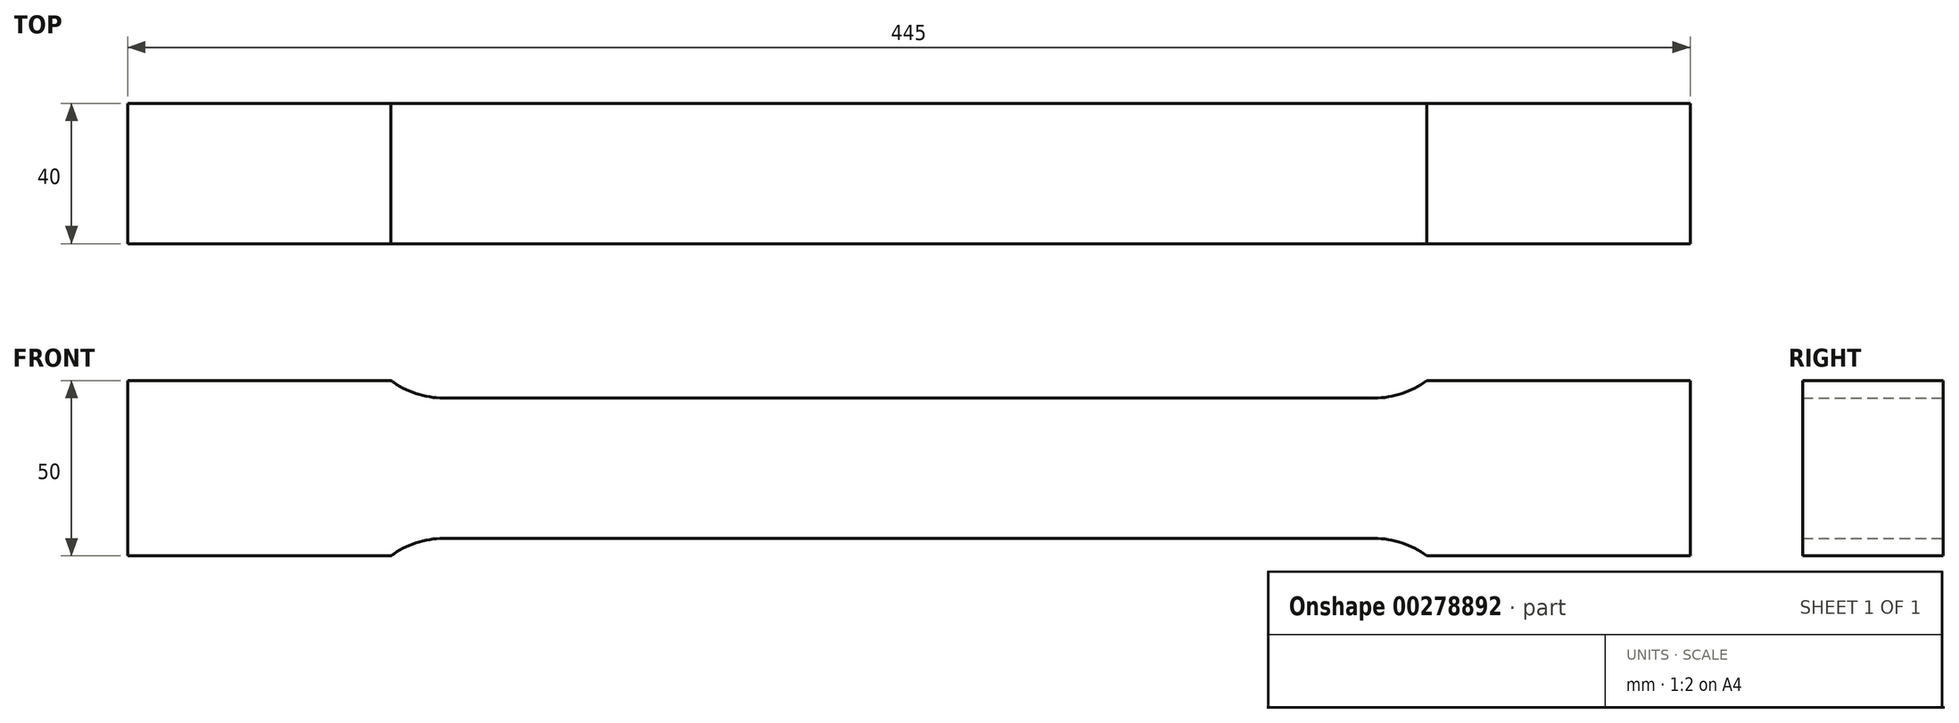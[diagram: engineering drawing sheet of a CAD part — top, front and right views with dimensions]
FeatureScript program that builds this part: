
annotation { "Feature Type Name" : "Feature", "Feature Type Description" : "" }
export const myFeature = defineFeature(function(context is Context, id is Id, definition is map)
    precondition{}
    {
        {
            var Q0;
            Q0=qCreatedBy(makeId("Front.planeOp"),FACE);
            var sketch = newSketch(context, id + "F0", { "sketchPlane" : qUnion([Q0])});
            skLineSegment(sketch, "E0", {"start": v(0, 20) * mm, "end": v(132.5, 20) * mm});
            skArc(sketch, "E1", {"start": v(132.5, 20) * mm, "mid": v(140.4, 21.28) * mm, "end": v(147.5, 25) * mm});
            skLineSegment(sketch, "E2", {"start": v(147.5, 25) * mm, "end": v(222.5, 25) * mm});
            skLineSegment(sketch, "E3", {"start": v(222.5, 25) * mm, "end": v(222.5, 0) * mm});
            skLineSegment(sketch, "E4.MirrorCS", {"start": v(0, -20) * mm, "end": v(132.5, -20) * mm});
            skLineSegment(sketch, "E5.MirrorCS", {"start": v(222.5, -25) * mm, "end": v(222.5, 0) * mm});
            skLineSegment(sketch, "E6.MirrorCS", {"start": v(147.5, -25) * mm, "end": v(222.5, -25) * mm});
            skArc(sketch, "E7.MirrorCS", {"start": v(132.5, -20) * mm, "mid": v(140.4, -21.28) * mm, "end": v(147.5, -25) * mm});
            skArc(sketch, "E8.MirrorCS", {"start": v(-132.5, -20) * mm, "mid": v(-140.4, -21.28) * mm, "end": v(-147.5, -25) * mm});
            skLineSegment(sketch, "E9.MirrorCS", {"start": v(-147.5, -25) * mm, "end": v(-222.5, -25) * mm});
            skArc(sketch, "E10.MirrorCS", {"start": v(-132.5, 20) * mm, "mid": v(-140.4, 21.28) * mm, "end": v(-147.5, 25) * mm});
            skLineSegment(sketch, "E11.MirrorCS", {"start": v(-147.5, 25) * mm, "end": v(-222.5, 25) * mm});
            skLineSegment(sketch, "E12.MirrorCS", {"start": v(-222.5, -25) * mm, "end": v(-222.5, 0) * mm});
            skLineSegment(sketch, "E13.MirrorCS", {"start": v(0, -20) * mm, "end": v(-132.5, -20) * mm});
            skLineSegment(sketch, "E14.MirrorCS", {"start": v(-222.5, 25) * mm, "end": v(-222.5, 0) * mm});
            skLineSegment(sketch, "E15.MirrorCS", {"start": v(0, 20) * mm, "end": v(-132.5, 20) * mm});
            skSolve(sketch);
        }
        {
            var Q0;
            Q0 = qSketchRegion(id + "F0", true);
            extrude(context, id + "F1", {"entities" : qUnion([Q0]), "endBound" : BoundingType.SYMMETRIC, "depth" : 40 * mm});
        }
    });
